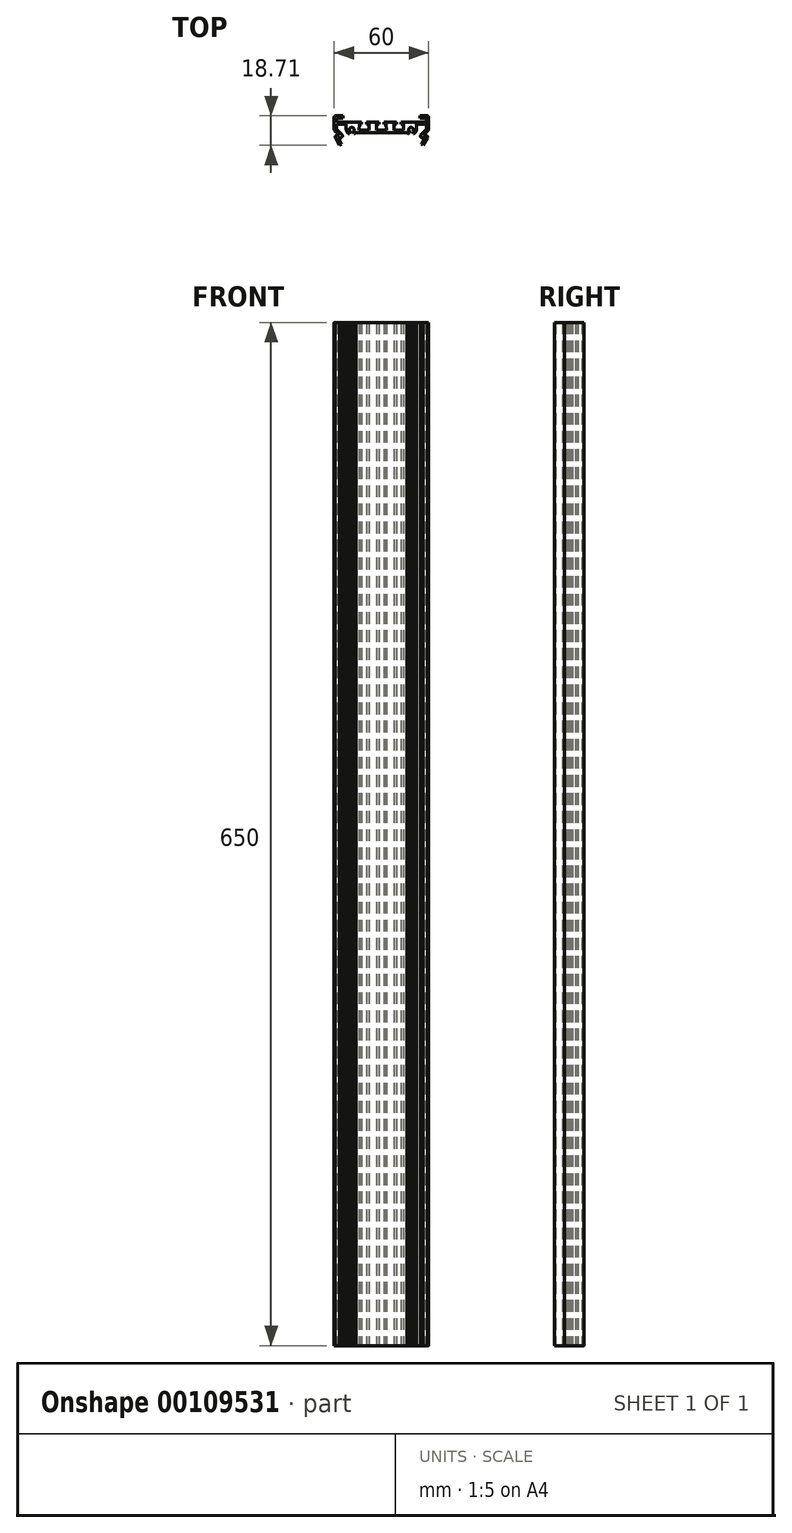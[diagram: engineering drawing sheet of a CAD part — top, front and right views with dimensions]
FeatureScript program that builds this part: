
annotation { "Feature Type Name" : "Feature", "Feature Type Description" : "" }
export const myFeature = defineFeature(function(context is Context, id is Id, definition is map)
    precondition{}
    {
        {
            var Q0;
            Q0=qCreatedBy(makeId("Top.planeOp"),FACE);
            var sketch = newSketch(context, id + "F0", { "sketchPlane" : qUnion([Q0])});
            skLineSegment(sketch, "E0.0.0", {"start": v(16.17, -2.6) * mm, "end": v(-16.17, -2.6) * mm});
            skArc(sketch, "E0.0.1", {"start": v(16.17, -2.6) * mm, "mid": v(16.7, -3.12) * mm, "end": v(17.32, -3.5) * mm});
            skLineSegment(sketch, "E0.0.2", {"start": v(17.32, -3.5) * mm, "end": v(18.1, -2.16) * mm});
            skArc(sketch, "E0.0.3", {"start": v(18.1, -2.16) * mm, "mid": v(18.85, 0.64) * mm, "end": v(19.6, -2.16) * mm});
            skLineSegment(sketch, "E0.0.4", {"start": v(19.6, -2.16) * mm, "end": v(20.38, -3.5) * mm});
            skArc(sketch, "E0.0.5", {"start": v(20.38, -3.5) * mm, "mid": v(21.82, -2.21) * mm, "end": v(22.35, -0.36) * mm});
            skLineSegment(sketch, "E0.0.6", {"start": v(22.35, -0.36) * mm, "end": v(22.35, 2.64) * mm});
            skLineSegment(sketch, "E0.0.7", {"start": v(22.35, 2.64) * mm, "end": v(28.65, 2.64) * mm});
            skLineSegment(sketch, "E0.0.8", {"start": v(28.65, 2.64) * mm, "end": v(28.65, -0.45) * mm});
            skLineSegment(sketch, "E0.0.9", {"start": v(28.65, -0.45) * mm, "end": v(25, -4.1) * mm});
            skArc(sketch, "E0.0.10", {"start": v(25, -4.1) * mm, "mid": v(24.78, -5.2) * mm, "end": v(25.7, -5.8) * mm});
            skLineSegment(sketch, "E0.0.11", {"start": v(25.7, -5.8) * mm, "end": v(27.71, -5.8) * mm});
            skLineSegment(sketch, "E0.0.12", {"start": v(27.71, -5.8) * mm, "end": v(25.37, -10.07) * mm});
            skLineSegment(sketch, "E0.0.13", {"start": v(25.37, -10.07) * mm, "end": v(26.55, -10.72) * mm});
            skLineSegment(sketch, "E0.0.14", {"start": v(26.55, -10.72) * mm, "end": v(29.18, -5.94) * mm});
            skArc(sketch, "E0.0.15", {"start": v(29.18, -5.94) * mm, "mid": v(29.17, -4.95) * mm, "end": v(28.3, -4.46) * mm});
            skLineSegment(sketch, "E0.0.16", {"start": v(28.3, -4.46) * mm, "end": v(27.75, -4.46) * mm});
            skArc(sketch, "E0.0.17", {"start": v(27.75, -4.46) * mm, "mid": v(27.3, -4.15) * mm, "end": v(27.4, -3.6) * mm});
            skLineSegment(sketch, "E0.0.18", {"start": v(27.4, -3.6) * mm, "end": v(29.7, -1.3) * mm});
            skArc(sketch, "E0.0.19", {"start": v(29.7, -1.3) * mm, "mid": v(29.92, -0.98) * mm, "end": v(30, -0.6) * mm});
            skLineSegment(sketch, "E0.0.20", {"start": v(30, -0.6) * mm, "end": v(30, 7) * mm});
            skArc(sketch, "E0.0.21", {"start": v(30, 7) * mm, "mid": v(29.7, 7.7) * mm, "end": v(29, 8) * mm});
            skLineSegment(sketch, "E0.0.22", {"start": v(29, 8) * mm, "end": v(24.5, 8) * mm});
            skLineSegment(sketch, "E0.0.23", {"start": v(24.5, 8) * mm, "end": v(24.5, 6.64) * mm});
            skLineSegment(sketch, "E0.0.24", {"start": v(24.5, 6.64) * mm, "end": v(28.65, 6.64) * mm});
            skLineSegment(sketch, "E0.0.25", {"start": v(28.65, 6.64) * mm, "end": v(28.65, 4) * mm});
            skLineSegment(sketch, "E0.0.26", {"start": v(28.65, 4) * mm, "end": v(12.5, 4) * mm});
            skLineSegment(sketch, "E0.0.27", {"start": v(12.5, 4) * mm, "end": v(12.5, 2.74) * mm});
            skLineSegment(sketch, "E0.0.28", {"start": v(12.5, 2.74) * mm, "end": v(14, 2.74) * mm});
            skLineSegment(sketch, "E0.0.29", {"start": v(14, 2.74) * mm, "end": v(14.12, -1.26) * mm});
            skLineSegment(sketch, "E0.0.30", {"start": v(14.13, -1.26) * mm, "end": v(7.88, -1.26) * mm});
            skLineSegment(sketch, "E0.0.31", {"start": v(7.88, -1.26) * mm, "end": v(8, 2.74) * mm});
            skLineSegment(sketch, "E0.0.32", {"start": v(8, 2.74) * mm, "end": v(9.5, 2.74) * mm});
            skLineSegment(sketch, "E0.0.33", {"start": v(9.5, 2.74) * mm, "end": v(9.5, 4) * mm});
            skLineSegment(sketch, "E0.0.34", {"start": v(9.5, 4) * mm, "end": v(1.5, 4) * mm});
            skLineSegment(sketch, "E0.0.35", {"start": v(1.5, 4) * mm, "end": v(1.5, 2.74) * mm});
            skLineSegment(sketch, "E0.0.36", {"start": v(1.5, 2.74) * mm, "end": v(3, 2.74) * mm});
            skLineSegment(sketch, "E0.0.37", {"start": v(3, 2.74) * mm, "end": v(3.12, -1.26) * mm});
            skLineSegment(sketch, "E0.0.38", {"start": v(3.13, -1.26) * mm, "end": v(-3.12, -1.26) * mm});
            skLineSegment(sketch, "E0.0.39", {"start": v(-3.12, -1.26) * mm, "end": v(-3, 2.74) * mm});
            skLineSegment(sketch, "E0.0.40", {"start": v(-3, 2.74) * mm, "end": v(-1.5, 2.74) * mm});
            skLineSegment(sketch, "E0.0.41", {"start": v(-1.5, 2.74) * mm, "end": v(-1.5, 4) * mm});
            skLineSegment(sketch, "E0.0.42", {"start": v(-1.5, 4) * mm, "end": v(-9.5, 4) * mm});
            skLineSegment(sketch, "E0.0.43", {"start": v(-9.5, 4) * mm, "end": v(-9.5, 2.74) * mm});
            skLineSegment(sketch, "E0.0.44", {"start": v(-9.5, 2.74) * mm, "end": v(-8, 2.74) * mm});
            skLineSegment(sketch, "E0.0.45", {"start": v(-8, 2.74) * mm, "end": v(-7.87, -1.26) * mm});
            skLineSegment(sketch, "E0.0.46", {"start": v(-7.87, -1.26) * mm, "end": v(-14.12, -1.26) * mm});
            skLineSegment(sketch, "E0.0.47", {"start": v(-14.12, -1.26) * mm, "end": v(-14, 2.74) * mm});
            skLineSegment(sketch, "E0.0.48", {"start": v(-14, 2.74) * mm, "end": v(-12.5, 2.74) * mm});
            skLineSegment(sketch, "E0.0.49", {"start": v(-12.5, 2.74) * mm, "end": v(-12.5, 4) * mm});
            skLineSegment(sketch, "E0.0.50", {"start": v(-12.5, 4) * mm, "end": v(-28.65, 4) * mm});
            skLineSegment(sketch, "E0.0.51", {"start": v(-28.65, 6.64) * mm, "end": v(-28.65, 4) * mm});
            skLineSegment(sketch, "E0.0.52", {"start": v(-24.5, 6.64) * mm, "end": v(-28.65, 6.64) * mm});
            skLineSegment(sketch, "E0.0.53", {"start": v(-24.5, 6.64) * mm, "end": v(-24.5, 8) * mm});
            skLineSegment(sketch, "E0.0.54", {"start": v(-24.5, 8) * mm, "end": v(-29, 8) * mm});
            skArc(sketch, "E0.0.55", {"start": v(-29, 8) * mm, "mid": v(-29.7, 7.7) * mm, "end": v(-30, 7) * mm});
            skLineSegment(sketch, "E0.0.56", {"start": v(-30, 7) * mm, "end": v(-30, -0.6) * mm});
            skArc(sketch, "E0.0.57", {"start": v(-30, -0.6) * mm, "mid": v(-29.92, -0.98) * mm, "end": v(-29.7, -1.3) * mm});
            skLineSegment(sketch, "E0.0.58", {"start": v(-29.7, -1.3) * mm, "end": v(-27.4, -3.6) * mm});
            skArc(sketch, "E0.0.59", {"start": v(-27.4, -3.6) * mm, "mid": v(-27.3, -4.15) * mm, "end": v(-27.75, -4.46) * mm});
            skLineSegment(sketch, "E0.0.60", {"start": v(-27.75, -4.46) * mm, "end": v(-28.3, -4.46) * mm});
            skArc(sketch, "E0.0.61", {"start": v(-28.3, -4.46) * mm, "mid": v(-29.17, -4.95) * mm, "end": v(-29.18, -5.94) * mm});
            skLineSegment(sketch, "E0.0.62", {"start": v(-29.18, -5.94) * mm, "end": v(-26.55, -10.72) * mm});
            skLineSegment(sketch, "E0.0.63", {"start": v(-26.55, -10.72) * mm, "end": v(-25.37, -10.07) * mm});
            skLineSegment(sketch, "E0.0.64", {"start": v(-25.37, -10.07) * mm, "end": v(-27.71, -5.8) * mm});
            skLineSegment(sketch, "E0.0.65", {"start": v(-25.7, -5.8) * mm, "end": v(-27.71, -5.8) * mm});
            skArc(sketch, "E0.0.66", {"start": v(-25.7, -5.8) * mm, "mid": v(-24.78, -5.2) * mm, "end": v(-25, -4.1) * mm});
            skLineSegment(sketch, "E0.0.67", {"start": v(-25, -4.1) * mm, "end": v(-28.65, -0.45) * mm});
            skLineSegment(sketch, "E0.0.68", {"start": v(-28.65, 2.64) * mm, "end": v(-28.65, -0.45) * mm});
            skLineSegment(sketch, "E0.0.69", {"start": v(-22.35, 2.64) * mm, "end": v(-28.65, 2.64) * mm});
            skLineSegment(sketch, "E0.0.70", {"start": v(-22.35, 2.64) * mm, "end": v(-22.35, -0.36) * mm});
            skArc(sketch, "E0.0.71", {"start": v(-22.35, -0.36) * mm, "mid": v(-21.82, -2.21) * mm, "end": v(-20.38, -3.5) * mm});
            skLineSegment(sketch, "E0.0.72", {"start": v(-20.38, -3.5) * mm, "end": v(-19.6, -2.16) * mm});
            skArc(sketch, "E0.0.73", {"start": v(-19.6, -2.16) * mm, "mid": v(-18.85, 0.64) * mm, "end": v(-18.1, -2.16) * mm});
            skLineSegment(sketch, "E0.0.74", {"start": v(-18.1, -2.16) * mm, "end": v(-17.32, -3.5) * mm});
            skArc(sketch, "E0.0.75", {"start": v(-17.32, -3.5) * mm, "mid": v(-16.7, -3.12) * mm, "end": v(-16.17, -2.6) * mm});
            skSolve(sketch);
        }
        {
            var Q0;
            Q0=qSketchRegion(id+"F0",true);
            extrude(context, id + "F1", {"entities" : qUnion([Q0]), "depth" : 650 * mm});
        }
    });
